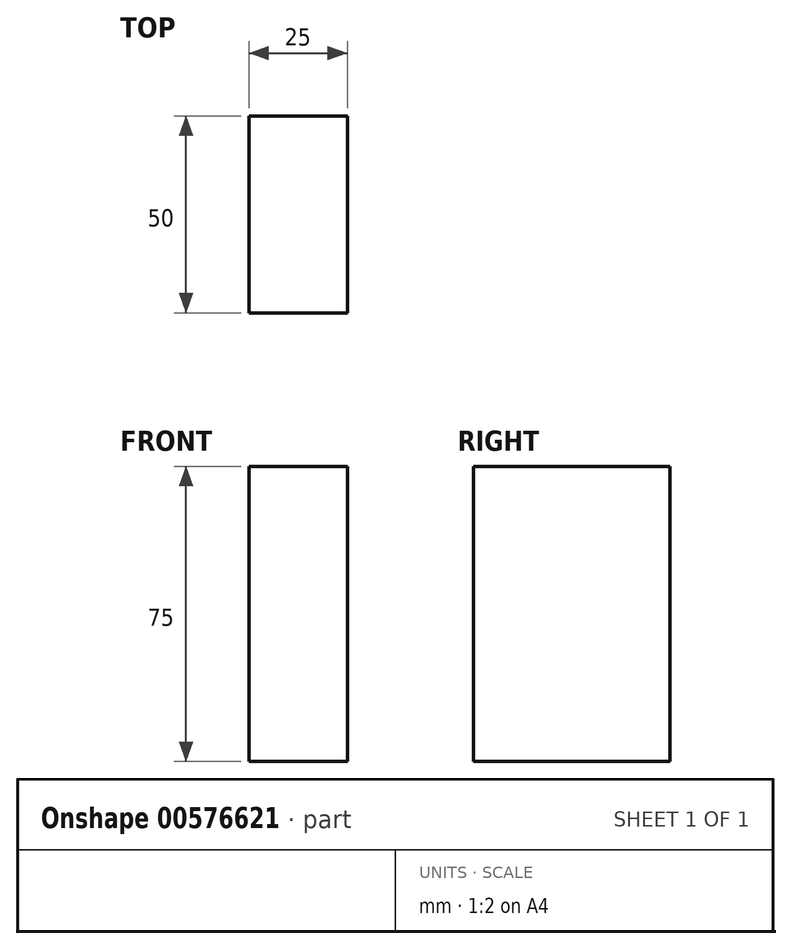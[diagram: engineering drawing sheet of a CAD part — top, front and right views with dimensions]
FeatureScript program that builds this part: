
annotation { "Feature Type Name" : "Feature", "Feature Type Description" : "" }
export const myFeature = defineFeature(function(context is Context, id is Id, definition is map)
    precondition{}
    {
        {
            var Q0;
            Q0=qCreatedBy(makeId("Top.planeOp"),FACE);
            var sketch = newSketch(context, id + "F0", { "sketchPlane" : qUnion([Q0])});
            skLineSegment(sketch, "E0.bottom", {"start": v(0, 0) * mm, "end": v(-25, 0) * mm});
            skLineSegment(sketch, "E0.top", {"start": v(0, 50) * mm, "end": v(-25, 50) * mm});
            skLineSegment(sketch, "E0.left", {"start": v(0, 0) * mm, "end": v(0, 50) * mm});
            skLineSegment(sketch, "E0.right", {"start": v(-25, 0) * mm, "end": v(-25, 50) * mm});
            skSolve(sketch);
        }
        {
            var Q0;
            Q0 = qSketchRegion(id + "F0", true);
            var Q1;
            Q1=makeQuery(id+"F0.imprint","IMPRINT",FACE,{"disambiguationData":[TD([[makeQuery(id+"F0.imprint","IMPRINT",EDGE,{"derivedFrom":sQuery(id+"F0.wireOp",EDGE,"E0.bottom")}),-1.0]])]});
            extrude(context, id + "F1", {"entities" : qUnion([Q0, Q1]), "depth" : 75 * mm, "offsetDistance" : 25 * mm});
        }
    });
